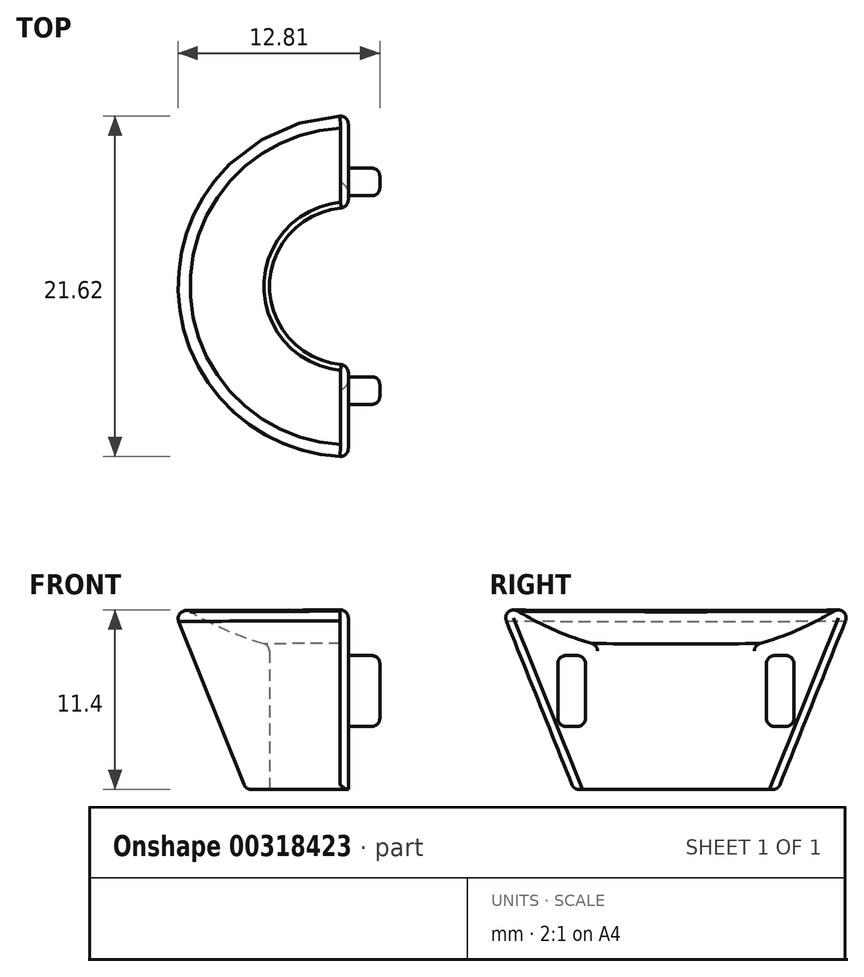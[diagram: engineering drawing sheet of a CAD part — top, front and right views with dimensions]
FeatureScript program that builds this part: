
annotation { "Feature Type Name" : "Feature", "Feature Type Description" : "" }
export const myFeature = defineFeature(function(context is Context, id is Id, definition is map)
    precondition{}
    {
        {
            var Q0;
            Q0=qCreatedBy(makeId("Top.planeOp"),FACE);
            var sketch = newSketch(context, id + "F0", { "sketchPlane" : qUnion([Q0])});
            skCircle(sketch, "E0", {"center": v(0, 0) * mm, "radius": 6.5 * mm});
            skSolve(sketch);
        }
        {
            var Q0;
            Q0=qCreatedBy(makeId("Top.planeOp"),FACE);
            cPlane(context, id + "F1", {"entities" : qUnion([Q0]), "cplaneType" : CPlaneType.OFFSET, "offset" : 15 * mm, "width" : 150 * mm, "height" : 150 * mm});
        }
        {
            var Q0;
            Q0=qCreatedBy(id+"F1.planeOp",FACE);
            var sketch = newSketch(context, id + "F2", { "sketchPlane" : qUnion([Q0])});
            skCircle(sketch, "E1", {"center": v(0, 0) * mm, "radius": 12.5 * mm});
            skSolve(sketch);
        }
        {
            var Q0;
            Q0=makeQuery(id+"F0.imprint","IMPRINT",FACE,{"disambiguationData":[TD([[makeQuery(id+"F0.imprint","IMPRINT",EDGE,{"derivedFrom":sQuery(id+"F0.wireOp",EDGE,"E0")}),1.0]])]});
            var Q1;
            Q1=makeQuery(id+"F2.imprint","IMPRINT",FACE,{"disambiguationData":[TD([[makeQuery(id+"F2.imprint","IMPRINT",EDGE,{"derivedFrom":sQuery(id+"F2.wireOp",EDGE,"E1")}),1.0]])]});
            loft(context, id + "F3", {"sheetProfilesArray" : [{ "sheetProfileEntities" : qUnion([Q0]) }, { "sheetProfileEntities" : qUnion([Q1]) }]});
        }
        {
            var Q0;
            Q0=makeQuery(id+"F3.opLoft","CAP_FACE",FACE,{"disambiguationData":[OSD([makeQuery(id+"F0.imprint","IMPRINT",FACE,{"disambiguationData":[TD([[makeQuery(id+"F0.imprint","IMPRINT",EDGE,{"derivedFrom":sQuery(id+"F0.wireOp",EDGE,"E0")}),1.0]])]})])],"isStart":true});
            var sketch = newSketch(context, id + "F4", { "sketchPlane" : qUnion([Q0])});
            skCircle(sketch, "E2", {"center": v(0, 0) * mm, "radius": 5 * mm});
            skSolve(sketch);
        }
        {
            var Q0;
            Q0=makeQuery(id+"F4.imprint","IMPRINT",FACE,{"disambiguationData":[TD([[makeQuery(id+"F4.imprint","IMPRINT",EDGE,{"derivedFrom":sQuery(id+"F4.wireOp",EDGE,"E2")}),1.0]])]});
            extrude(context, id + "F5", {"entities" : qUnion([Q0]), "operationType" : NewBodyOperationType.REMOVE, "oppositeDirection" : true, "depth" : 10 * mm});
        }
        {
            var Q0;
            Q0=qCreatedBy(makeId("Front.planeOp"),FACE);
            var sketch = newSketch(context, id + "F6", { "sketchPlane" : qUnion([Q0])});
            skArc(sketch, "E3", {"start": v(0.03, 47.5) * mm, "mid": v(-19.5, 28.09) * mm, "end": v(-0.14, 8.5) * mm});
            skLineSegment(sketch, "E4", {"start": v(-0.14, 8.5) * mm, "end": v(0.03, 47.5) * mm});
            skSolve(sketch);
        }
        {
            var Q0;
            Q0=makeQuery(id+"F6.imprint","IMPRINT",FACE,{"disambiguationData":[TD([[makeQuery(id+"F6.imprint","IMPRINT",EDGE,{"derivedFrom":sQuery(id+"F6.wireOp",EDGE,"E3")}),1.0]])]});
            var Q1;
            Q1=sQuery(id+"F6.wireOp",EDGE,"E4");
            revolve(context, id + "F7", {"operationType" : NewBodyOperationType.REMOVE, "entities" : qUnion([Q0]), "axis" : qUnion([Q1]), "revolveType" : RevolveType.FULL});
        }
        {
            var Q0;
            Q0=qCreatedBy(makeId("Front.planeOp"),FACE);
            var sketch = newSketch(context, id + "F8", { "sketchPlane" : qUnion([Q0])});
            skLineSegment(sketch, "E5.bottom", {"start": v(0, 0) * mm, "end": v(15, 0) * mm});
            skLineSegment(sketch, "E5.top", {"start": v(0, 15) * mm, "end": v(15, 15) * mm});
            skLineSegment(sketch, "E5.left", {"start": v(0, 0) * mm, "end": v(0, 15) * mm});
            skLineSegment(sketch, "E5.right", {"start": v(15, 0) * mm, "end": v(15, 15) * mm});
            skSolve(sketch);
        }
        {
            var Q0;
            Q0=makeQuery(id+"F8.imprint","IMPRINT",FACE,{"disambiguationData":[TD([[makeQuery(id+"F8.imprint","IMPRINT",EDGE,{"derivedFrom":sQuery(id+"F8.wireOp",EDGE,"E5.bottom")}),1.0]])]});
            extrude(context, id + "F9", {"entities" : qUnion([Q0]), "operationType" : NewBodyOperationType.REMOVE, "depth" : 25 * mm, "hasSecondDirection" : true, "secondDirectionOppositeDirection" : true, "secondDirectionDepth" : 25 * mm});
        }
        {
            var Q0;
            Q0=makeQuery(id+"FPjt2AgAj65mRvz_1.boolean.opBoolean","SPLIT",FACE,{"disambiguationData":[OD(0.0)],"derivedFrom":makeQuery(id+"F9.boolean.opBoolean","COPY",FACE,{"derivedFrom":makeQuery(id+"F9.opExtrude","SWEPT_FACE",FACE,{"disambiguationData":[OSD([sQuery(id+"F8.wireOp",EDGE,"E5.left")])]})})});
            var sketch = newSketch(context, id + "F10", { "sketchPlane" : qUnion([Q0])});
            skLineSegment(sketch, "E6.bottom", {"start": v(-6.25, 8.5) * mm, "end": v(-7, 8.5) * mm});
            skLineSegment(sketch, "E6.top", {"start": v(-6.25, 4) * mm, "end": v(-7, 4) * mm});
            skLineSegment(sketch, "E6.left", {"start": v(-5.75, 8) * mm, "end": v(-5.75, 4.5) * mm});
            skLineSegment(sketch, "E6.right", {"start": v(-7.5, 8) * mm, "end": v(-7.5, 4.5) * mm});
            skPoint(sketch, "E7.visualSharp", {"position": v(-7.5, 8.5) * mm});
            skArc(sketch, "E7.filletArc", {"start": v(-7, 8.5) * mm, "mid": v(-7.35, 8.35) * mm, "end": v(-7.5, 8) * mm});
            skPoint(sketch, "E8.visualSharp", {"position": v(-5.75, 8.5) * mm});
            skArc(sketch, "E8.filletArc", {"start": v(-5.75, 8) * mm, "mid": v(-5.9, 8.35) * mm, "end": v(-6.25, 8.5) * mm});
            skPoint(sketch, "E9.visualSharp", {"position": v(-5.75, 4) * mm});
            skArc(sketch, "E9.filletArc", {"start": v(-6.25, 4) * mm, "mid": v(-5.9, 4.15) * mm, "end": v(-5.75, 4.5) * mm});
            skPoint(sketch, "E10.visualSharp", {"position": v(-7.5, 4) * mm});
            skArc(sketch, "E10.filletArc", {"start": v(-7.5, 4.5) * mm, "mid": v(-7.35, 4.15) * mm, "end": v(-7, 4) * mm});
            skLineSegment(sketch, "E11.MirrorCS", {"start": v(5.75, 8) * mm, "end": v(5.75, 4.5) * mm});
            skArc(sketch, "E12.MirrorCS", {"start": v(5.75, 8) * mm, "mid": v(5.9, 8.35) * mm, "end": v(6.25, 8.5) * mm});
            skLineSegment(sketch, "E13.MirrorCS", {"start": v(6.25, 8.5) * mm, "end": v(7, 8.5) * mm});
            skArc(sketch, "E14.MirrorCS", {"start": v(7, 8.5) * mm, "mid": v(7.35, 8.35) * mm, "end": v(7.5, 8) * mm});
            skLineSegment(sketch, "E15.MirrorCS", {"start": v(7.5, 8) * mm, "end": v(7.5, 4.5) * mm});
            skPoint(sketch, "E16.MirrorP", {"position": v(7.5, 4) * mm});
            skArc(sketch, "E17.MirrorCS", {"start": v(7.5, 4.5) * mm, "mid": v(7.35, 4.15) * mm, "end": v(7, 4) * mm});
            skLineSegment(sketch, "E18.MirrorCS", {"start": v(6.25, 4) * mm, "end": v(7, 4) * mm});
            skArc(sketch, "E19.MirrorCS", {"start": v(6.25, 4) * mm, "mid": v(5.9, 4.15) * mm, "end": v(5.75, 4.5) * mm});
            skSolve(sketch);
        }
        {
            var Q0;
            Q0=makeQuery(id+"F10.imprint","IMPRINT",FACE,{"disambiguationData":[TD([[makeQuery(id+"F10.imprint","IMPRINT",EDGE,{"derivedFrom":sQuery(id+"F10.wireOp",EDGE,"E6.bottom")}),1.0]])]});
            var Q1;
            Q1=makeQuery(id+"F10.imprint","IMPRINT",FACE,{"disambiguationData":[TD([[makeQuery(id+"F10.imprint","IMPRINT",EDGE,{"derivedFrom":sQuery(id+"F10.wireOp",EDGE,"E11.MirrorCS")}),1.0]])]});
            extrude(context, id + "F11", {"entities" : qUnion([Q0, Q1]), "operationType" : NewBodyOperationType.ADD, "depth" : 2 * mm});
        }
        {
            var Q0;
            Q0=makeQuery(id+"F7.boolean.opBoolean","INTERSECT",EDGE,{"derivedFrom":[makeQuery(id+"F3.opLoft","SWEPT_FACE",FACE,{"disambiguationData":[OSD([sQuery(id+"F0.wireOp",EDGE,"E0"),sQuery(id+"F2.wireOp",EDGE,"E1")])]}),makeQuery(id+"F7.opRevolve","SWEPT_FACE",FACE,{"disambiguationData":[OSD([sQuery(id+"F6.wireOp",EDGE,"E3")])]})]});
            var Q1;
            Q1=makeQuery(id+"F3.opLoft","MID_CAP_EDGE",EDGE,{"disambiguationData":[OSD([sQuery(id+"F0.wireOp",EDGE,"E0")])],"capPos":0.0});
            var Q2;
            Q2=makeQuery(id+"F5.boolean.opBoolean","COPY",EDGE,{"derivedFrom":makeQuery(id+"F5.opExtrude","CAP_EDGE",EDGE,{"disambiguationData":[OSD([sQuery(id+"F4.wireOp",EDGE,"E2")])],"isStart":true})});
            var Q3;
            Q3=makeQuery(id+"F9.boolean.opBoolean","INTERSECT",EDGE,{"disambiguationData":[OD(0.0)],"derivedFrom":[makeQuery(id+"F5.boolean.opBoolean","COPY",FACE,{"derivedFrom":makeQuery(id+"F5.opExtrude","SWEPT_FACE",FACE,{"disambiguationData":[OSD([sQuery(id+"F4.wireOp",EDGE,"E2")])]})}),makeQuery(id+"F9.opExtrude","SWEPT_FACE",FACE,{"disambiguationData":[OSD([sQuery(id+"F8.wireOp",EDGE,"E5.left")])]})]});
            var Q4;
            Q4=makeQuery(id+"F9.boolean.opBoolean","INTERSECT",EDGE,{"disambiguationData":[OD(1.0)],"derivedFrom":[makeQuery(id+"F5.boolean.opBoolean","COPY",FACE,{"derivedFrom":makeQuery(id+"F5.opExtrude","SWEPT_FACE",FACE,{"disambiguationData":[OSD([sQuery(id+"F4.wireOp",EDGE,"E2")])]})}),makeQuery(id+"F9.opExtrude","SWEPT_FACE",FACE,{"disambiguationData":[OSD([sQuery(id+"F8.wireOp",EDGE,"E5.left")])]})]});
            var Q5;
            Q5=makeQuery(id+"F7.boolean.opBoolean","INTERSECT",EDGE,{"derivedFrom":[makeQuery(id+"F5.boolean.opBoolean","COPY",FACE,{"derivedFrom":makeQuery(id+"F5.opExtrude","SWEPT_FACE",FACE,{"disambiguationData":[OSD([sQuery(id+"F4.wireOp",EDGE,"E2")])]})}),makeQuery(id+"F7.opRevolve","SWEPT_FACE",FACE,{"disambiguationData":[OSD([sQuery(id+"F6.wireOp",EDGE,"E3")])]})]});
            var Q6;
            Q6=makeQuery(id+"F9.boolean.opBoolean","INTERSECT",EDGE,{"disambiguationData":[OD(1.0)],"derivedFrom":[makeQuery(id+"F7.boolean.opBoolean","COPY",FACE,{"derivedFrom":makeQuery(id+"F7.opRevolve","SWEPT_FACE",FACE,{"disambiguationData":[OSD([sQuery(id+"F6.wireOp",EDGE,"E3")])]})}),makeQuery(id+"F9.opExtrude","SWEPT_FACE",FACE,{"disambiguationData":[OSD([sQuery(id+"F8.wireOp",EDGE,"E5.left")])]})]});
            var Q7;
            Q7=makeQuery(id+"F9.boolean.opBoolean","INTERSECT",EDGE,{"disambiguationData":[OD(0.0)],"derivedFrom":[makeQuery(id+"F7.boolean.opBoolean","COPY",FACE,{"derivedFrom":makeQuery(id+"F7.opRevolve","SWEPT_FACE",FACE,{"disambiguationData":[OSD([sQuery(id+"F6.wireOp",EDGE,"E3")])]})}),makeQuery(id+"F9.opExtrude","SWEPT_FACE",FACE,{"disambiguationData":[OSD([sQuery(id+"F8.wireOp",EDGE,"E5.left")])]})]});
            var Q8;
            Q8=makeQuery(id+"F11.opExtrude","CAP_EDGE",EDGE,{"disambiguationData":[OSD([sQuery(id+"F10.wireOp",EDGE,"E6.right")])],"isStart":false});
            var Q9;
            Q9=makeQuery(id+"F11.opExtrude","CAP_EDGE",EDGE,{"disambiguationData":[OSD([sQuery(id+"F10.wireOp",EDGE,"E6.left")])],"isStart":false});
            var Q10;
            Q10=makeQuery(id+"F11.opExtrude","CAP_EDGE",EDGE,{"disambiguationData":[OSD([sQuery(id+"F10.wireOp",EDGE,"E11.MirrorCS")])],"isStart":false});
            var Q11;
            Q11=makeQuery(id+"F9.boolean.opBoolean","INTERSECT",EDGE,{"disambiguationData":[OD(0.0)],"derivedFrom":[makeQuery(id+"F3.opLoft","SWEPT_FACE",FACE,{"disambiguationData":[OSD([sQuery(id+"F0.wireOp",EDGE,"E0"),sQuery(id+"F2.wireOp",EDGE,"E1")])]}),makeQuery(id+"F9.opExtrude","SWEPT_FACE",FACE,{"disambiguationData":[OSD([sQuery(id+"F8.wireOp",EDGE,"E5.left")])]})]});
            var Q12;
            Q12=makeQuery(id+"F9.boolean.opBoolean","INTERSECT",EDGE,{"disambiguationData":[OD(1.0)],"derivedFrom":[makeQuery(id+"F3.opLoft","SWEPT_FACE",FACE,{"disambiguationData":[OSD([sQuery(id+"F0.wireOp",EDGE,"E0"),sQuery(id+"F2.wireOp",EDGE,"E1")])]}),makeQuery(id+"F9.opExtrude","SWEPT_FACE",FACE,{"disambiguationData":[OSD([sQuery(id+"F8.wireOp",EDGE,"E5.left")])]})]});
            fillet(context, id + "F12", {"entities" : qUnion([Q0, Q1, Q2, Q3, Q4, Q5, Q6, Q7, Q8, Q9, Q10, Q11, Q12]), "radius" : .5 * mm, "tangentPropagation" : true, "allowEdgeOverflow" : false});
        }
    });
